# Revit family: StopValve-(Built-in,Exposedpart)-Vitra-XLineSeries-A41445
name_source: partatom
category: Plumbing Fixtures
revit_build: Autodesk Revit 2017 (Build: 20160225_1515(x64)
units: mm (PartAtom-declared; Revit-internal decimal feet)

## family parameters
Cut with Voids When Loaded = No
Host = Face
OmniClass Number = 23.45.55.17
OmniClass Title = Mixing Faucets
Part Type = Normal
Room Calculation Point = No
Round Connector Dimension = Use Diameter
Shared = Yes

## types (4) — shared parameters
BIMobject category = Sanitary - Taps & Mixers
CW Connection = Yes
Connection Diameter (mm) = 24 mm  [stored 0.0787402 ft]
Default Elevation = 850 mm  [stored 2.78871 ft]
Depth(mm) = 103 mm  [stored 0.337927 ft]
Description = X-Line Built-in Stop Valve (Exposed Part)
Design country = Turkey
HW Connection = Yes
Height(mm) = 90 mm
Hot Water Supply (max.) = 80 °C
Hot Water temperature, factory set to = 38 °C
IFC Classification = Valve
Main Material = Brass
Manufacturer = Vitra
Manufacturer name = Vitra
Masterformat 2014 Code = 33 12 16
Masterformat 2014 Description = Water Utility Distribution Valves
Min. flow pressure of = 0.5 bar
MountingType = Wall-mounted (exposed part)
NBS Referans Description = Valves
Nominal height = 0.000
Nominal width = 0.000
Number Of Connections = 1 mm  [stored 0.00328084 ft]
OmniClass Code = 23-31 11 00
OmniClass Description = Faucets
Product Type = Built-in Stop Valve(exposed part)
Product certification = https://vitraglobal.com
Product family = X-Line
Product group = Stop Valve (exposed part)
Range of Hot Water Supply = 5 - 65 °C
Range of flow pressure = 1 - 5 bar
Test Pressure = 16 bar
UNSPSC Code = 301815
UNSPSC Description = Sanitary ware
URL = https://vitraglobal.com
Uniclass 1.4 Code = L7117
Uniclass 1.4 Description = Valves for water supply/distribution
Uniclass 2.0 Description = Valves
Uniclass 2015 Name = Valve products
Uniformat II Code = 22 40 00
Uniformat II Description = Plumbing Fixture
Weight Net (kg) = 0,330
Width(mm) = 80 mm  [stored 0.262467 ft]
Youtube = https://www.youtube.com
zero-valued in all types: CWFU, Cost, HWFU, WFU

## per-type parameters (varying)
| type | Article No. (default) | Brand | Coating Material | Color | Installation instructions | Model | Product SKU | Product data url | Technical description | Warranty Period (Year) |
| Stopvalve(Exposedpart)-X-LineSeries(Chrome)-A41445 | A41445 | Artema | Chrome | Chrome |  | A41445 | A41445 | https://www.vitra.com.tr | https://www.vitra.com.tr | 10 Years |
| Stopvalve(Exposedpart)-X-LineSeries(Gold)-A4144523 | A4144523 | Artema | Gold | Gold |  | A4144523 | A4144523 | https://www.vitra.com.tr | https://www.vitra.com.tr | 10 Years |
| Stopvalve(Exposedpart)-X-LineSeries(Chrome)-A41445EXP | A41445EXP | Vitra | Chrome | Chrome | https://cdn.vitra.com.tr | A41445EXP | A41445EXP | https://www.vitraglobal.com | https://www.vitraglobal.com | 7 Years |
| Stopvalve(Exposedpart)-X-LineSeries(Gold)-A4144523EXP | A4144523EXP | Vitra | Gold | Gold | https://cdn.vitra.com.tr | A4144523EXP | A4144523EXP | https://www.vitraglobal.com | https://www.vitraglobal.com | 7 Years |

note: [stored X ft] marks values corroborated as IEEE doubles in the binary element streams (Revit-internal decimal feet)

## geometry (parser evidence)
native form markers: Sweep x3
no freeform markers — native parametric forms only
